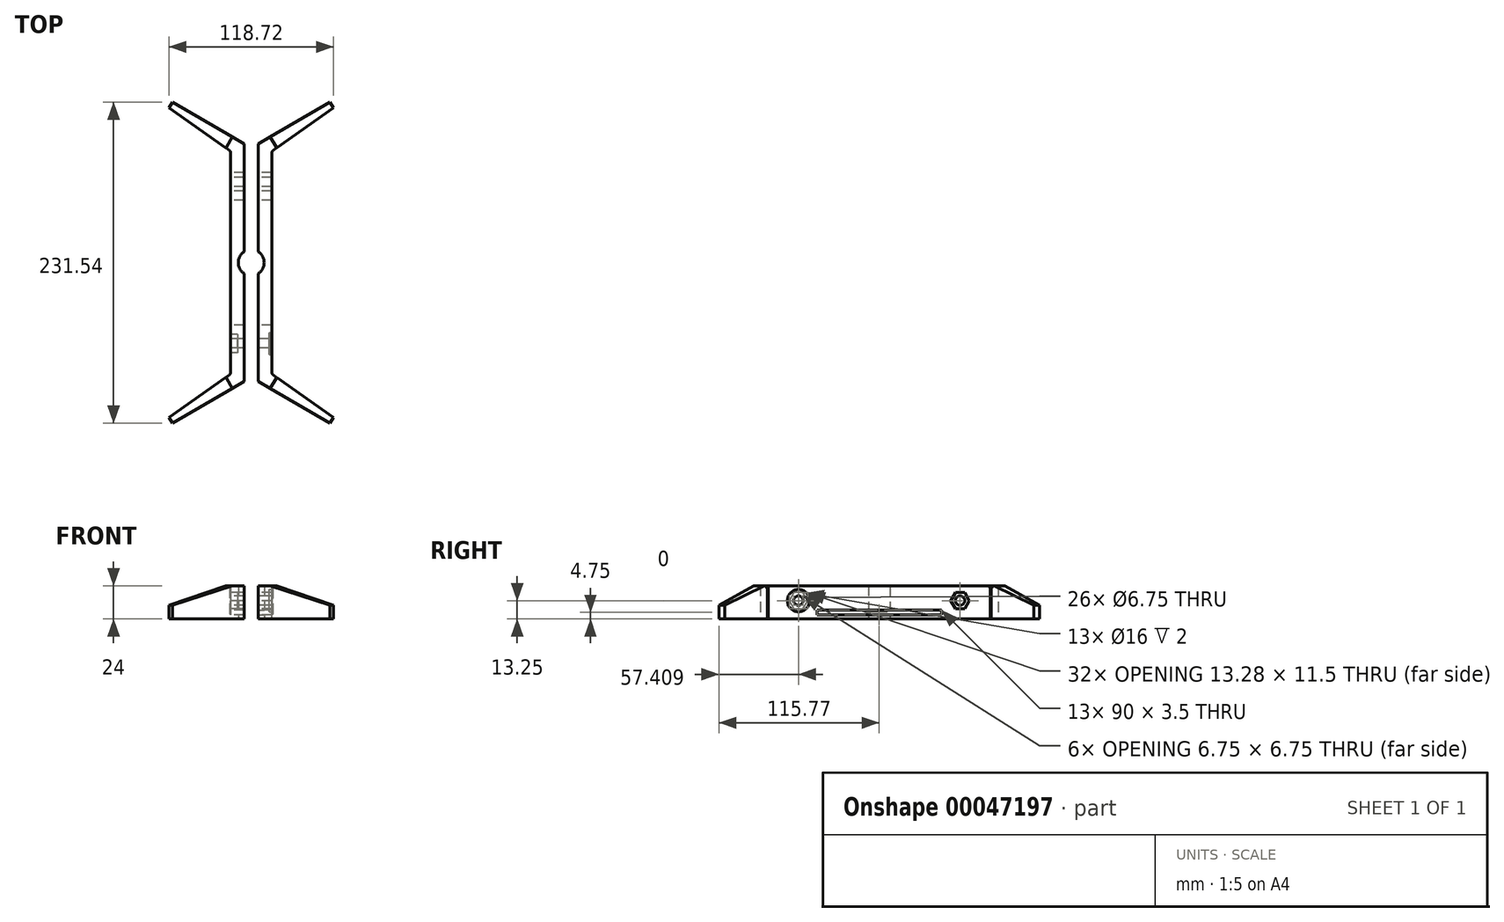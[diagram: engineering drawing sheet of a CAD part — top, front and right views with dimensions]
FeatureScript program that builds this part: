
annotation { "Feature Type Name" : "Feature", "Feature Type Description" : "" }
export const myFeature = defineFeature(function(context is Context, id is Id, definition is map)
    precondition{}
    {
        {
            assignVariable(context, id + "F0", {"name" : "Height", "anyValue" : 24});
        }
        {
            assignVariable(context, id + "F1", {"name" : "StabilizerLength", "anyValue" : 60});
        }
        {
            assignVariable(context, id + "F2", {"name" : "Thickness", "anyValue" : 10});
        }
        {
            var Q0;
            Q0=qCreatedBy(makeId("Top.planeOp"),FACE);
            var sketch = newSketch(context, id + "F3", { "sketchPlane" : qUnion([Q0])});
            skLineSegment(sketch, "E0", {"start": v(-15, -80) * mm, "end": v(-15, 80) * mm});
            skLineSegment(sketch, "E1", {"start": v(-15, 80) * mm, "end": v(-5, 80) * mm});
            skCircle(sketch, "E2", {"center": v(0, 0) * mm, "radius": 9.38 * mm});
            skLineSegment(sketch, "E3", {"start": v(-5, 80) * mm, "end": v(-5, 7.93) * mm});
            skLineSegment(sketch, "E4", {"start": v(-5, -7.93) * mm, "end": v(-5, -80) * mm});
            skLineSegment(sketch, "E5", {"start": v(0, 113.6) * mm, "end": v(0, -106.5) * mm, "construction": true});
            skPoint(sketch, "E6", {"position": v(-15, 0) * mm});
            skLineSegment(sketch, "E7.MirrorCS", {"start": v(15, -80) * mm, "end": v(15, 80) * mm});
            skPoint(sketch, "E8.MirrorP", {"position": v(15, 0) * mm});
            skLineSegment(sketch, "E9.MirrorCS", {"start": v(5, -7.93) * mm, "end": v(5, -80) * mm});
            skLineSegment(sketch, "E10.MirrorCS", {"start": v(5, 80) * mm, "end": v(5, 7.93) * mm});
            skLineSegment(sketch, "E11.MirrorCS", {"start": v(15, 80) * mm, "end": v(5, 80) * mm});
            skLineSegment(sketch, "E12.MirrorCS", {"start": v(15, -80) * mm, "end": v(5, -80) * mm});
            skLineSegment(sketch, "E13", {"start": v(-108.04, 0) * mm, "end": v(106.5, 0) * mm, "construction": true});
            skLineSegment(sketch, "E14", {"start": v(-15, -80) * mm, "end": v(-5, -80) * mm});
            skLineSegment(sketch, "E15", {"start": v(-15, 80) * mm, "end": v(-61.96, 107.11) * mm});
            skLineSegment(sketch, "E16", {"start": v(-61.96, 107.11) * mm, "end": v(-56.96, 115.77) * mm});
            skLineSegment(sketch, "E17", {"start": v(-5, 80) * mm, "end": v(-5, 85.77) * mm});
            skLineSegment(sketch, "E18", {"start": v(-5, 85.77) * mm, "end": v(-56.96, 115.77) * mm});
            skLineSegment(sketch, "E19.MirrorCS", {"start": v(-5, -80) * mm, "end": v(-5, -85.77) * mm});
            skLineSegment(sketch, "E20.MirrorCS", {"start": v(-5, -85.77) * mm, "end": v(-56.96, -115.77) * mm});
            skLineSegment(sketch, "E21.MirrorCS", {"start": v(-15, -80) * mm, "end": v(-61.96, -107.11) * mm});
            skLineSegment(sketch, "E22.MirrorCS", {"start": v(-61.96, -107.11) * mm, "end": v(-56.96, -115.77) * mm});
            skLineSegment(sketch, "E23.MirrorCS", {"start": v(61.96, 107.11) * mm, "end": v(56.96, 115.77) * mm});
            skLineSegment(sketch, "E24.MirrorCS", {"start": v(5, 85.77) * mm, "end": v(56.96, 115.77) * mm});
            skLineSegment(sketch, "E25.MirrorCS", {"start": v(15, 80) * mm, "end": v(61.96, 107.11) * mm});
            skLineSegment(sketch, "E26.MirrorCS", {"start": v(5, 80) * mm, "end": v(5, 85.77) * mm});
            skLineSegment(sketch, "E27.MirrorCS", {"start": v(5, -80) * mm, "end": v(5, -85.77) * mm});
            skLineSegment(sketch, "E28.MirrorCS", {"start": v(61.96, -107.11) * mm, "end": v(56.96, -115.77) * mm});
            skLineSegment(sketch, "E29.MirrorCS", {"start": v(5, -85.77) * mm, "end": v(56.96, -115.77) * mm});
            skLineSegment(sketch, "E30.MirrorCS", {"start": v(15, -80) * mm, "end": v(61.96, -107.11) * mm});
            skSolve(sketch);
        }
        {
            var Q0;
            Q0=makeQuery(id+"F3.imprint","IMPRINT",FACE,{"disambiguationData":[TD([[makeQuery(id+"F3.imprint","IMPRINT",EDGE,{"derivedFrom":sQuery(id+"F3.wireOp",EDGE,"E1")}),1.0]])]});
            var Q1;
            Q1=makeQuery(id+"F3.imprint","IMPRINT",FACE,{"disambiguationData":[TD([[makeQuery(id+"F3.imprint","IMPRINT",EDGE,{"derivedFrom":sQuery(id+"F3.wireOp",EDGE,"E0")}),-1.0]])]});
            var Q2;
            Q2=makeQuery(id+"F3.imprint","IMPRINT",FACE,{"disambiguationData":[TD([[makeQuery(id+"F3.imprint","IMPRINT",EDGE,{"derivedFrom":sQuery(id+"F3.wireOp",EDGE,"E14")}),-1.0]])]});
            var Q3;
            Q3=makeQuery(id+"F3.imprint","IMPRINT",FACE,{"disambiguationData":[TD([[makeQuery(id+"F3.imprint","IMPRINT",EDGE,{"derivedFrom":sQuery(id+"F3.wireOp",EDGE,"E12.MirrorCS")}),1.0]])]});
            var Q4;
            Q4=makeQuery(id+"F3.imprint","IMPRINT",FACE,{"disambiguationData":[TD([[makeQuery(id+"F3.imprint","IMPRINT",EDGE,{"derivedFrom":sQuery(id+"F3.wireOp",EDGE,"E7.MirrorCS")}),1.0]])]});
            var Q5;
            Q5=makeQuery(id+"F3.imprint","IMPRINT",FACE,{"disambiguationData":[TD([[makeQuery(id+"F3.imprint","IMPRINT",EDGE,{"derivedFrom":sQuery(id+"F3.wireOp",EDGE,"E11.MirrorCS")}),-1.0]])]});
            extrude(context, id + "F4", {"entities" : qUnion([Q0, Q1, Q2, Q3, Q4, Q5]), "depth" : (getVariable(context, 'Height')) * mm});
        }
        {
            var Q0;
            Q0=makeQuery(id+"F4.opExtrude","SWEPT_FACE",FACE,{"disambiguationData":[OSD([sQuery(id+"F3.wireOp",EDGE,"E0")])]});
            var sketch = newSketch(context, id + "F5", { "sketchPlane" : qUnion([Q0])});
            skLineSegment(sketch, "E31.0", {"start": v(80, 0) * mm, "end": v(-80, 0) * mm, "construction": true});
            skLineSegment(sketch, "E31.1", {"start": v(-80, 24) * mm, "end": v(-80, 0) * mm, "construction": true});
            skLineSegment(sketch, "E31.2", {"start": v(80, 24) * mm, "end": v(-80, 24) * mm, "construction": true});
            skLineSegment(sketch, "E31.3", {"start": v(80, 24) * mm, "end": v(80, 0) * mm, "construction": true});
            skLineSegment(sketch, "E32", {"start": v(-45, 6.5) * mm, "end": v(-45, 3) * mm});
            skLineSegment(sketch, "E33", {"start": v(-45, 3) * mm, "end": v(45, 3) * mm});
            skLineSegment(sketch, "E34", {"start": v(45, 3) * mm, "end": v(45, 6.5) * mm});
            skLineSegment(sketch, "E35", {"start": v(45, 6.5) * mm, "end": v(-45, 6.5) * mm});
            skPoint(sketch, "E36", {"position": v(0, 3) * mm});
            skCircle(sketch, "E37.cCircle", {"center": v(58.36, 13.25) * mm, "radius": 5.75 * mm, "construction": true});
            skLineSegment(sketch, "E37.0", {"start": v(61.68, 19) * mm, "end": v(65, 13.25) * mm});
            skLineSegment(sketch, "E37.1", {"start": v(65, 13.25) * mm, "end": v(61.68, 7.5) * mm});
            skLineSegment(sketch, "E37.2", {"start": v(61.68, 7.5) * mm, "end": v(55.04, 7.5) * mm});
            skLineSegment(sketch, "E37.3", {"start": v(55.04, 7.5) * mm, "end": v(51.72, 13.25) * mm});
            skLineSegment(sketch, "E37.4", {"start": v(51.72, 13.25) * mm, "end": v(55.04, 19) * mm});
            skLineSegment(sketch, "E37.5", {"start": v(55.04, 19) * mm, "end": v(61.68, 19) * mm});
            skPoint(sketch, "E37.0.midPoint", {"position": v(63.34, 16.13) * mm});
            skLineSegment(sketch, "E38", {"start": v(0, 46.42) * mm, "end": v(0, -19.84) * mm, "construction": true});
            skPoint(sketch, "E39.MirrorP", {"position": v(-63.34, 16.13) * mm});
            skLineSegment(sketch, "E40.MirrorCS", {"start": v(-55.04, 19) * mm, "end": v(-61.68, 19) * mm});
            skLineSegment(sketch, "E41.MirrorCS", {"start": v(-51.72, 13.25) * mm, "end": v(-55.04, 19) * mm});
            skLineSegment(sketch, "E42.MirrorCS", {"start": v(-61.68, 7.5) * mm, "end": v(-55.04, 7.5) * mm});
            skCircle(sketch, "E43.MirrorC", {"center": v(-58.36, 13.25) * mm, "radius": 5.75 * mm, "construction": true});
            skLineSegment(sketch, "E44.MirrorCS", {"start": v(-61.68, 19) * mm, "end": v(-65, 13.25) * mm});
            skLineSegment(sketch, "E45.MirrorCS", {"start": v(-55.04, 7.5) * mm, "end": v(-51.72, 13.25) * mm});
            skLineSegment(sketch, "E46.MirrorCS", {"start": v(-65, 13.25) * mm, "end": v(-61.68, 7.5) * mm});
            skCircle(sketch, "E47", {"center": v(58.36, 13.25) * mm, "radius": 3.38 * mm});
            skCircle(sketch, "E48.MirrorC", {"center": v(-58.36, 13.25) * mm, "radius": 3.38 * mm});
            skSolve(sketch);
        }
        {
            var Q0;
            Q0=makeQuery(id+"F5.imprint","IMPRINT",FACE,{"disambiguationData":[TD([[makeQuery(id+"F5.imprint","IMPRINT",EDGE,{"derivedFrom":sQuery(id+"F5.wireOp",EDGE,"E32")}),1.0]])]});
            var Q1;
            Q1=makeQuery(id+"F5.imprint","IMPRINT",FACE,{"disambiguationData":[TD([[makeQuery(id+"F5.imprint","IMPRINT",EDGE,{"derivedFrom":sQuery(id+"F5.wireOp",EDGE,"E48.MirrorC")}),-1.0]])]});
            var Q2;
            Q2=makeQuery(id+"F5.imprint","IMPRINT",FACE,{"disambiguationData":[TD([[makeQuery(id+"F5.imprint","IMPRINT",EDGE,{"derivedFrom":sQuery(id+"F5.wireOp",EDGE,"E47")}),1.0]])]});
            extrude(context, id + "F6", {"entities" : qUnion([Q0, Q1, Q2]), "operationType" : NewBodyOperationType.REMOVE, "endBound" : BoundingType.THROUGH_ALL, "oppositeDirection" : true, "depth" : 25 * mm});
        }
        {
            var Q0;
            Q0=makeQuery(id+"F5.imprint","IMPRINT",FACE,{"disambiguationData":[TD([[makeQuery(id+"F5.imprint","IMPRINT",EDGE,{"derivedFrom":sQuery(id+"F5.wireOp",EDGE,"E37.0")}),-1.0]])]});
            var Q1;
            Q1=makeQuery(id+"F5.imprint","IMPRINT",FACE,{"disambiguationData":[TD([[makeQuery(id+"F5.imprint","IMPRINT",EDGE,{"derivedFrom":sQuery(id+"F5.wireOp",EDGE,"E40.MirrorCS")}),1.0]])]});
            extrude(context, id + "F7", {"entities" : qUnion([Q0, Q1]), "operationType" : NewBodyOperationType.REMOVE, "oppositeDirection" : true, "depth" : 5 * mm});
        }
        {
            var Q0;
            Q0=makeQuery(id+"F4.opExtrude","SWEPT_FACE",FACE,{"disambiguationData":[OSD([sQuery(id+"F3.wireOp",EDGE,"E7.MirrorCS")])]});
            var sketch = newSketch(context, id + "F8", { "sketchPlane" : qUnion([Q0])});
            skCircle(sketch, "E49.4", {"center": v(58.36, 13.25) * mm, "radius": 3.38 * mm, "construction": true});
            skCircle(sketch, "E49.5", {"center": v(-58.36, 13.25) * mm, "radius": 3.38 * mm, "construction": true});
            skCircle(sketch, "E50", {"center": v(-58.36, 13.25) * mm, "radius": 8 * mm});
            skLineSegment(sketch, "E51", {"start": v(0, 51.19) * mm, "end": v(0, -36.04) * mm, "construction": true});
            skCircle(sketch, "E52.MirrorC", {"center": v(58.36, 13.25) * mm, "radius": 8 * mm});
            skSolve(sketch);
        }
        {
            var Q0;
            Q0=makeQuery(id+"F8.imprint","IMPRINT",FACE,{"disambiguationData":[TD([[makeQuery(id+"F8.imprint","IMPRINT",EDGE,{"derivedFrom":sQuery(id+"F8.wireOp",EDGE,"E50")}),1.0]])]});
            var Q1;
            Q1=makeQuery(id+"F8.imprint","IMPRINT",FACE,{"disambiguationData":[TD([[makeQuery(id+"F8.imprint","IMPRINT",EDGE,{"derivedFrom":sQuery(id+"F8.wireOp",EDGE,"E52.MirrorC")}),-1.0]])]});
            extrude(context, id + "F9", {"entities" : qUnion([Q0, Q1]), "operationType" : NewBodyOperationType.REMOVE, "oppositeDirection" : true, "depth" : 2 * mm});
        }
        {
            var Q0;
            Q0=makeQuery(id+"F4.opExtrude","CAP_EDGE",EDGE,{"disambiguationData":[OSD([sQuery(id+"F3.wireOp",EDGE,"E22.MirrorCS")])],"isStart":false});
            var Q1;
            Q1=makeQuery(id+"F4.opExtrude","CAP_EDGE",EDGE,{"disambiguationData":[OSD([sQuery(id+"F3.wireOp",EDGE,"E16")])],"isStart":false});
            var Q2;
            Q2=makeQuery(id+"F4.opExtrude","CAP_EDGE",EDGE,{"disambiguationData":[OSD([sQuery(id+"F3.wireOp",EDGE,"E23.MirrorCS")])],"isStart":false});
            var Q3;
            Q3=makeQuery(id+"F4.opExtrude","CAP_EDGE",EDGE,{"disambiguationData":[OSD([sQuery(id+"F3.wireOp",EDGE,"E28.MirrorCS")])],"isStart":false});
            chamfer(context, id + "F10", {"entities" : qUnion([Q0, Q1, Q2, Q3]), "chamferType" : ChamferType.TWO_OFFSETS, "width1" : (getVariable(context, 'StabilizerLength') - getVariable(context, 'Thickness')) * mm, "oppositeDirection" : false, "width2" : (getVariable(context, 'Height') - getVariable(context, 'Thickness')) * mm, "tangentPropagation" : true});
        }
        {
            var Q0;
            Q0=makeQuery(id+"F4.opExtrude","SWEPT_FACE",FACE,{"disambiguationData":[OSD([sQuery(id+"F3.wireOp",EDGE,"E15")])]});
            var Q1;
            Q1=makeQuery(id+"F4.opExtrude","SWEPT_EDGE",EDGE,{"disambiguationData":[OSD([sQuery(id+"F3.wireOp",EDGE,"E17"),sQuery(id+"F3.wireOp",EDGE,"E18")])]});
            revolve(context, id + "F11", {"operationType" : NewBodyOperationType.REMOVE, "entities" : qUnion([Q0]), "axis" : qUnion([Q1]), "revolveType" : RevolveType.ONE_DIRECTION, "angle" : 5 * degree});
        }
        {
            var Q0;
            Q0=makeQuery(id+"F4.opExtrude","SWEPT_FACE",FACE,{"disambiguationData":[OSD([sQuery(id+"F3.wireOp",EDGE,"E25.MirrorCS")])]});
            var Q1;
            Q1=makeQuery(id+"F4.opExtrude","SWEPT_EDGE",EDGE,{"disambiguationData":[OSD([sQuery(id+"F3.wireOp",EDGE,"E24.MirrorCS"),sQuery(id+"F3.wireOp",EDGE,"E26.MirrorCS")])]});
            revolve(context, id + "F12", {"operationType" : NewBodyOperationType.REMOVE, "entities" : qUnion([Q0]), "axis" : qUnion([Q1]), "revolveType" : RevolveType.ONE_DIRECTION, "oppositeDirection" : true, "angle" : 5 * degree});
        }
        {
            var Q0;
            Q0=makeQuery(id+"F4.opExtrude","SWEPT_FACE",FACE,{"disambiguationData":[OSD([sQuery(id+"F3.wireOp",EDGE,"E30.MirrorCS")])]});
            var Q1;
            Q1=makeQuery(id+"F4.opExtrude","SWEPT_EDGE",EDGE,{"disambiguationData":[OSD([sQuery(id+"F3.wireOp",EDGE,"E27.MirrorCS"),sQuery(id+"F3.wireOp",EDGE,"E29.MirrorCS")])]});
            revolve(context, id + "F13", {"operationType" : NewBodyOperationType.REMOVE, "entities" : qUnion([Q0]), "axis" : qUnion([Q1]), "revolveType" : RevolveType.ONE_DIRECTION, "angle" : 5 * degree});
        }
        {
            var Q0;
            Q0=makeQuery(id+"F4.opExtrude","SWEPT_FACE",FACE,{"disambiguationData":[OSD([sQuery(id+"F3.wireOp",EDGE,"E21.MirrorCS")])]});
            var Q1;
            Q1=makeQuery(id+"F4.opExtrude","SWEPT_EDGE",EDGE,{"disambiguationData":[OSD([sQuery(id+"F3.wireOp",EDGE,"E19.MirrorCS"),sQuery(id+"F3.wireOp",EDGE,"E20.MirrorCS")])]});
            revolve(context, id + "F14", {"operationType" : NewBodyOperationType.REMOVE, "entities" : qUnion([Q0]), "axis" : qUnion([Q1]), "revolveType" : RevolveType.ONE_DIRECTION, "oppositeDirection" : true, "angle" : 5 * degree});
        }
        {
            var Q0;
            Q0=makeQuery(id+"F4.opExtrude","SWEPT_EDGE",EDGE,{"disambiguationData":[OSD([sQuery(id+"F3.wireOp",EDGE,"E7.MirrorCS"),sQuery(id+"F3.wireOp",EDGE,"E12.MirrorCS")])]});
            var Q1;
            Q1=makeQuery(id+"F4.opExtrude","CAP_EDGE",EDGE,{"disambiguationData":[OSD([sQuery(id+"F3.wireOp",EDGE,"E12.MirrorCS")])],"isStart":false});
            var Q2;
            Q2=makeQuery(id+"F4.opExtrude","CAP_EDGE",EDGE,{"disambiguationData":[OSD([sQuery(id+"F3.wireOp",EDGE,"E7.MirrorCS")])],"isStart":false});
            var Q3;
            Q3=makeQuery(id+"F4.opExtrude","CAP_EDGE",EDGE,{"disambiguationData":[OSD([sQuery(id+"F3.wireOp",EDGE,"E11.MirrorCS")])],"isStart":false});
            var Q4;
            Q4=makeQuery(id+"F4.opExtrude","SWEPT_EDGE",EDGE,{"disambiguationData":[OSD([sQuery(id+"F3.wireOp",EDGE,"E7.MirrorCS"),sQuery(id+"F3.wireOp",EDGE,"E11.MirrorCS")])]});
            var Q5;
            Q5=makeQuery(id+"F4.opExtrude","CAP_EDGE",EDGE,{"disambiguationData":[OSD([sQuery(id+"F3.wireOp",EDGE,"49nATwem-sjRw-i11F-duBF-eeFVnD8axQ5k")])],"isStart":false});
            var Q6;
            Q6=makeQuery(id+"F4.opExtrude","SWEPT_EDGE",EDGE,{"disambiguationData":[OSD([sQuery(id+"F3.wireOp",EDGE,"E0"),sQuery(id+"F3.wireOp",EDGE,"49nATwem-sjRw-i11F-duBF-eeFVnD8axQ5k")])]});
            var Q7;
            Q7=makeQuery(id+"F4.opExtrude","CAP_EDGE",EDGE,{"disambiguationData":[OSD([sQuery(id+"F3.wireOp",EDGE,"E0")])],"isStart":false});
            var Q8;
            Q8=makeQuery(id+"F4.opExtrude","CAP_EDGE",EDGE,{"disambiguationData":[OSD([sQuery(id+"F3.wireOp",EDGE,"E1")])],"isStart":false});
            var Q9;
            Q9=makeQuery(id+"F4.opExtrude","SWEPT_EDGE",EDGE,{"disambiguationData":[OSD([sQuery(id+"F3.wireOp",EDGE,"E0"),sQuery(id+"F3.wireOp",EDGE,"E1")])]});
            fillet(context, id + "F15", {"entities" : qUnion([Q0, Q1, Q2, Q3, Q4, Q5, Q6, Q7, Q8, Q9]), "radius" : 2 * mm, "tangentPropagation" : true, "allowEdgeOverflow" : false});
        }
    });
